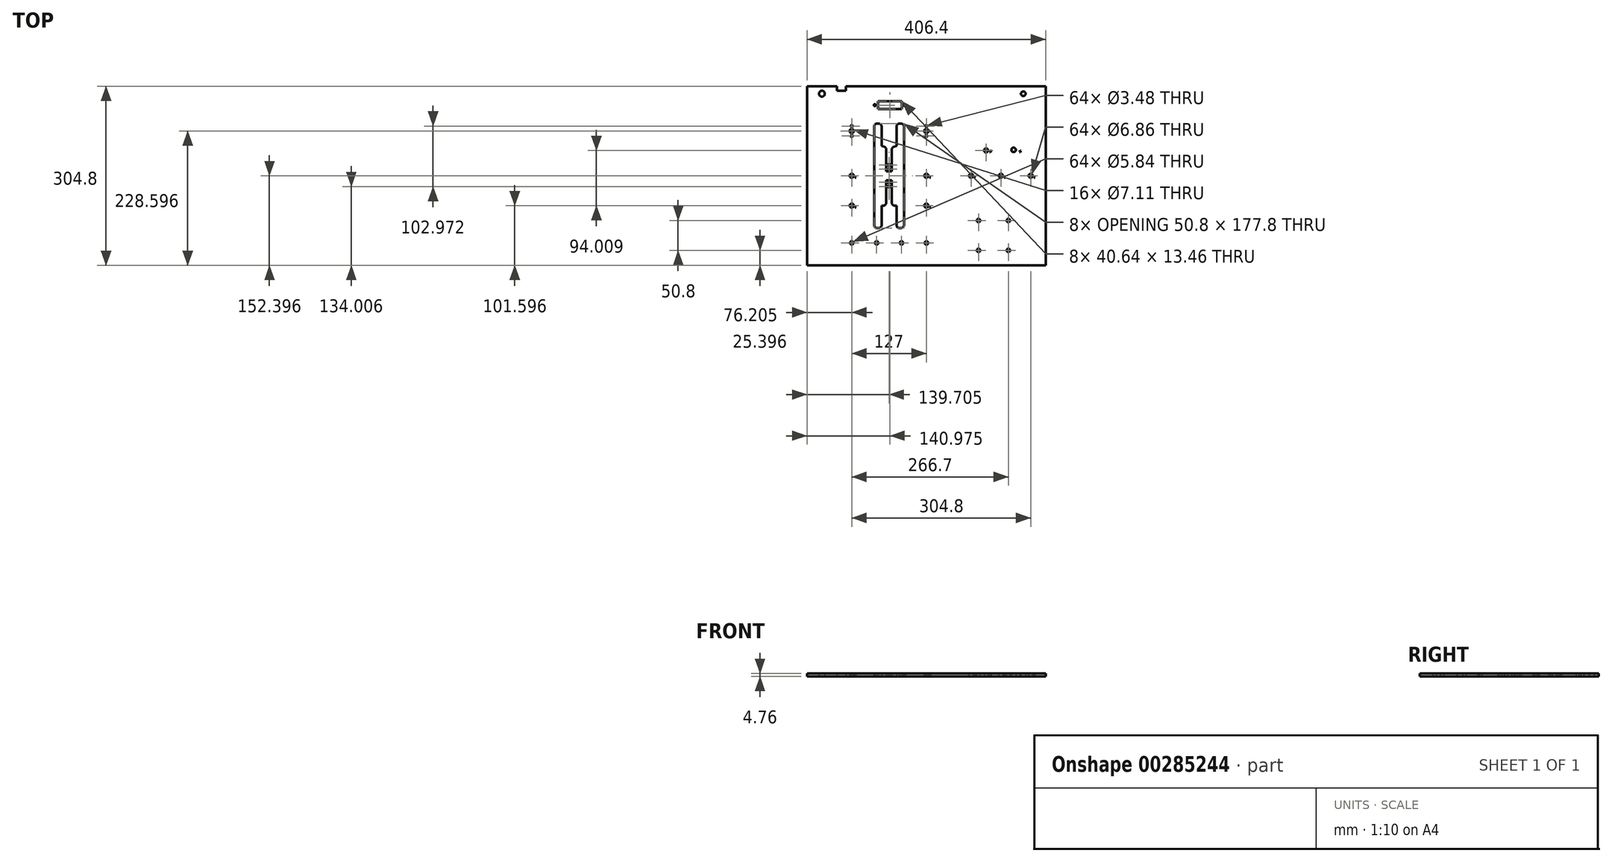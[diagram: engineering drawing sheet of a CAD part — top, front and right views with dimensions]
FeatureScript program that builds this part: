
annotation { "Feature Type Name" : "Feature", "Feature Type Description" : "" }
export const myFeature = defineFeature(function(context is Context, id is Id, definition is map)
    precondition{}
    {
        {
            var Q0;
            Q0=qCreatedBy(makeId("Top.planeOp"),FACE);
            var sketch = newSketch(context, id + "F0", { "sketchPlane" : qUnion([Q0])});
            skLineSegment(sketch, "E0.bottom", {"start": v(-218.92, 163.26) * mm, "end": v(187.48, 163.26) * mm});
            skLineSegment(sketch, "E0.top", {"start": v(-218.92, -141.54) * mm, "end": v(187.48, -141.54) * mm});
            skLineSegment(sketch, "E0.left", {"start": v(-218.92, 163.26) * mm, "end": v(-218.92, -141.54) * mm});
            skLineSegment(sketch, "E0.right", {"start": v(187.48, 163.26) * mm, "end": v(187.48, -141.54) * mm});
            skSolve(sketch);
        }
        {
            var Q0;
            Q0=makeQuery(id+"F0.imprint","IMPRINT",FACE,{"disambiguationData":[TD([[makeQuery(id+"F0.imprint","IMPRINT",EDGE,{"derivedFrom":sQuery(id+"F0.wireOp",EDGE,"E0.bottom")}),-1.0]])]});
            extrude(context, id + "F1", {"entities" : qUnion([Q0]), "depth" : 4.76 * mm});
        }
        {
            var Q0;
            Q0=qCreatedBy(makeId("Top.planeOp"),FACE);
            var sketch = newSketch(context, id + "F2", { "sketchPlane" : qUnion([Q0])});
            skCircle(sketch, "E1", {"center": v(-142.72, 87.06) * mm, "radius": 12.2 * mm, "construction": true});
            skCircle(sketch, "E2", {"center": v(-142.72, 95.44) * mm, "radius": 1.74 * mm});
            skCircle(sketch, "E3", {"center": v(-142.72, 78.67) * mm, "radius": 1.74 * mm});
            skLineSegment(sketch, "E4", {"start": v(-142.72, 87.06) * mm, "end": v(-142.72, -142.08) * mm, "construction": true});
            skCircle(sketch, "E5", {"center": v(-142.72, 10.86) * mm, "radius": 3.43 * mm});
            skCircle(sketch, "E6", {"center": v(-142.72, 87.06) * mm, "radius": 3.56 * mm});
            skLineSegment(sketch, "E7.top", {"start": v(-136.6, 8) * mm, "end": v(-135.36, 7.72) * mm});
            skLineSegment(sketch, "E7.left", {"start": v(-136.6, 8) * mm, "end": v(-136.67, 7.67) * mm});
            skLineSegment(sketch, "E7.right", {"start": v(-135.36, 7.72) * mm, "end": v(-135.44, 7.38) * mm});
            skLineSegment(sketch, "E8", {"start": v(-136.67, 7.67) * mm, "end": v(-135.44, 7.38) * mm});
            skCircle(sketch, "E9.0.1.0", {"center": v(-142.72, -39.94) * mm, "radius": 3.43 * mm});
            skLineSegment(sketch, "E9.0.1.1", {"start": v(-136.6, -42.8) * mm, "end": v(-135.36, -43.08) * mm});
            skLineSegment(sketch, "E9.0.1.2", {"start": v(-136.67, -43.13) * mm, "end": v(-135.44, -43.42) * mm});
            skLineSegment(sketch, "E9.0.1.3", {"start": v(-135.36, -43.08) * mm, "end": v(-135.44, -43.42) * mm});
            skLineSegment(sketch, "E9.0.1.4", {"start": v(-136.6, -42.8) * mm, "end": v(-136.67, -43.13) * mm});
            skLineSegment(sketch, "E9.direction1", {"start": v(-142.72, 10.86) * mm, "end": v(-117.32, 10.86) * mm, "construction": true});
            skLineSegment(sketch, "E9.direction2", {"start": v(-142.72, 10.86) * mm, "end": v(-142.72, -39.94) * mm, "construction": true});
            skCircle(sketch, "E10.1.0.0", {"center": v(-15.72, -39.94) * mm, "radius": 3.43 * mm});
            skCircle(sketch, "E10.1.0.1", {"center": v(-15.72, 87.06) * mm, "radius": 3.56 * mm});
            skCircle(sketch, "E10.1.0.2", {"center": v(-15.72, 10.86) * mm, "radius": 3.43 * mm});
            skLineSegment(sketch, "E10.1.0.3", {"start": v(-15.72, 87.06) * mm, "end": v(-15.72, -142.08) * mm, "construction": true});
            skCircle(sketch, "E10.1.0.4", {"center": v(-15.72, 87.06) * mm, "radius": 12.2 * mm, "construction": true});
            skLineSegment(sketch, "E10.1.0.5", {"start": v(-15.72, 10.86) * mm, "end": v(9.68, 10.86) * mm, "construction": true});
            skLineSegment(sketch, "E10.1.0.6", {"start": v(-15.72, 10.86) * mm, "end": v(-15.72, -39.94) * mm, "construction": true});
            skCircle(sketch, "E10.1.0.7", {"center": v(-15.72, 78.67) * mm, "radius": 1.74 * mm});
            skCircle(sketch, "E10.1.0.8", {"center": v(-15.72, 95.44) * mm, "radius": 1.74 * mm});
            skLineSegment(sketch, "E10.1.0.9", {"start": v(-8.36, 7.72) * mm, "end": v(-8.44, 7.38) * mm});
            skLineSegment(sketch, "E10.1.0.10", {"start": v(-9.67, 7.67) * mm, "end": v(-8.44, 7.38) * mm});
            skLineSegment(sketch, "E10.1.0.11", {"start": v(-9.6, 8) * mm, "end": v(-8.36, 7.72) * mm});
            skLineSegment(sketch, "E10.1.0.12", {"start": v(-8.36, -43.08) * mm, "end": v(-8.44, -43.42) * mm});
            skLineSegment(sketch, "E10.1.0.13", {"start": v(-9.6, 8) * mm, "end": v(-9.67, 7.67) * mm});
            skLineSegment(sketch, "E10.1.0.14", {"start": v(-9.6, -42.8) * mm, "end": v(-9.67, -43.13) * mm});
            skLineSegment(sketch, "E10.1.0.15", {"start": v(-9.6, -42.8) * mm, "end": v(-8.36, -43.08) * mm});
            skLineSegment(sketch, "E10.1.0.16", {"start": v(-9.67, -43.13) * mm, "end": v(-8.44, -43.42) * mm});
            skLineSegment(sketch, "E10.direction1", {"start": v(-142.72, -142.08) * mm, "end": v(-15.72, -142.08) * mm, "construction": true});
            skLineSegment(sketch, "E11.bottom", {"start": v(-168.12, 163.26) * mm, "end": v(-152.88, 163.26) * mm});
            skLineSegment(sketch, "E11.top", {"start": v(-168.12, 155.38) * mm, "end": v(-152.88, 155.38) * mm});
            skLineSegment(sketch, "E11.left", {"start": v(-168.12, 163.26) * mm, "end": v(-168.12, 155.38) * mm});
            skLineSegment(sketch, "E11.right", {"start": v(-152.88, 163.26) * mm, "end": v(-152.88, 155.38) * mm});
            skCircle(sketch, "E12", {"center": v(-193.52, 150.56) * mm, "radius": 4.95 * mm});
            skLineSegment(sketch, "E13.1.0.0", {"start": v(67.84, 7.72) * mm, "end": v(67.76, 7.38) * mm});
            skLineSegment(sketch, "E13.1.0.1", {"start": v(66.6, 8) * mm, "end": v(66.53, 7.67) * mm});
            skCircle(sketch, "E13.1.0.2", {"center": v(60.48, 10.86) * mm, "radius": 3.43 * mm});
            skLineSegment(sketch, "E13.1.0.3", {"start": v(66.6, 8) * mm, "end": v(67.84, 7.72) * mm});
            skLineSegment(sketch, "E13.1.0.4", {"start": v(66.53, 7.67) * mm, "end": v(67.76, 7.38) * mm});
            skLineSegment(sketch, "E13.direction1", {"start": v(-15.72, 10.86) * mm, "end": v(60.48, 10.86) * mm, "construction": true});
            skLineSegment(sketch, "E14.1.0.0", {"start": v(117.33, 7.67) * mm, "end": v(118.56, 7.38) * mm});
            skLineSegment(sketch, "E14.1.0.1", {"start": v(35.08, 10.86) * mm, "end": v(111.28, 10.86) * mm, "construction": true});
            skLineSegment(sketch, "E14.1.0.2", {"start": v(118.64, 7.72) * mm, "end": v(118.56, 7.38) * mm});
            skLineSegment(sketch, "E14.1.0.3", {"start": v(117.4, 8) * mm, "end": v(117.33, 7.67) * mm});
            skLineSegment(sketch, "E14.1.0.4", {"start": v(117.4, 8) * mm, "end": v(118.64, 7.72) * mm});
            skCircle(sketch, "E14.1.0.5", {"center": v(111.28, 10.86) * mm, "radius": 3.43 * mm});
            skLineSegment(sketch, "E14.2.0.0", {"start": v(168.13, 7.67) * mm, "end": v(169.36, 7.38) * mm});
            skLineSegment(sketch, "E14.2.0.1", {"start": v(85.88, 10.86) * mm, "end": v(162.08, 10.86) * mm, "construction": true});
            skLineSegment(sketch, "E14.2.0.2", {"start": v(169.44, 7.72) * mm, "end": v(169.36, 7.38) * mm});
            skLineSegment(sketch, "E14.2.0.3", {"start": v(168.2, 8) * mm, "end": v(168.13, 7.67) * mm});
            skLineSegment(sketch, "E14.2.0.4", {"start": v(168.2, 8) * mm, "end": v(169.44, 7.72) * mm});
            skCircle(sketch, "E14.2.0.5", {"center": v(162.08, 10.86) * mm, "radius": 3.43 * mm});
            skLineSegment(sketch, "E14.direction1", {"start": v(-15.72, 10.86) * mm, "end": v(35.08, 10.86) * mm, "construction": true});
            skLineSegment(sketch, "E15.1.0.0", {"start": v(92.8, 53.94) * mm, "end": v(94.04, 53.66) * mm});
            skLineSegment(sketch, "E15.1.0.2", {"start": v(94.04, 53.66) * mm, "end": v(93.41, 50.93) * mm});
            skLineSegment(sketch, "E15.1.0.3", {"start": v(92.8, 53.94) * mm, "end": v(92.17, 51.22) * mm});
            skLineSegment(sketch, "E15.1.0.4", {"start": v(92.17, 51.22) * mm, "end": v(93.41, 50.93) * mm});
            skCircle(sketch, "E15.1.0.5", {"center": v(86.05, 54.06) * mm, "radius": 3.43 * mm});
            skLineSegment(sketch, "E15.2.0.0", {"start": v(143.6, 53.94) * mm, "end": v(144.84, 53.66) * mm});
            skLineSegment(sketch, "E15.2.0.1", {"start": v(56.7, 54.98) * mm, "end": v(132.9, 54.98) * mm, "construction": true});
            skLineSegment(sketch, "E15.2.0.2", {"start": v(144.84, 53.66) * mm, "end": v(144.21, 50.93) * mm});
            skLineSegment(sketch, "E15.2.0.3", {"start": v(143.6, 53.94) * mm, "end": v(142.97, 51.22) * mm});
            skLineSegment(sketch, "E15.2.0.4", {"start": v(142.97, 51.22) * mm, "end": v(144.21, 50.93) * mm});
            skCircle(sketch, "E15.2.0.5", {"center": v(132.9, 54.98) * mm, "radius": 3.81 * mm});
            skLineSegment(sketch, "E16.bottom", {"start": v(-99.54, 99.76) * mm, "end": v(-97, 99.76) * mm});
            skLineSegment(sketch, "E16.top", {"start": v(-99.54, -78.04) * mm, "end": v(-97, -78.04) * mm});
            skLineSegment(sketch, "E16.left", {"start": v(-104.62, 94.68) * mm, "end": v(-104.62, -72.96) * mm});
            skLineSegment(sketch, "E16.right", {"start": v(-53.82, 94.68) * mm, "end": v(-53.82, -72.96) * mm});
            skLineSegment(sketch, "E17.left", {"start": v(-91.92, 94.68) * mm, "end": v(-91.92, 61.66) * mm});
            skLineSegment(sketch, "E17.right", {"start": v(-66.52, 94.68) * mm, "end": v(-66.52, 61.66) * mm});
            skLineSegment(sketch, "E18.left", {"start": v(-91.92, 76.83) * mm, "end": v(-91.92, 77.38) * mm, "construction": true});
            skLineSegment(sketch, "E18.right", {"start": v(-104.62, 76.83) * mm, "end": v(-104.62, 77.38) * mm, "construction": true});
            skLineSegment(sketch, "E19.trimOffspring", {"start": v(-61.44, 99.76) * mm, "end": v(-58.9, 99.76) * mm});
            skLineSegment(sketch, "E20.bottom", {"start": v(-83.88, 18.48) * mm, "end": v(-74.55, 18.48) * mm});
            skLineSegment(sketch, "E20.top", {"start": v(-83.88, 3.24) * mm, "end": v(-74.55, 3.24) * mm});
            skLineSegment(sketch, "E21", {"start": v(-83.88, 18.48) * mm, "end": v(-83.88, 55.4) * mm});
            skLineSegment(sketch, "E22", {"start": v(-87.43, 60.24) * mm, "end": v(-91.92, 61.66) * mm});
            skLineSegment(sketch, "E23", {"start": v(-79.22, 18.48) * mm, "end": v(-79.22, 3.24) * mm, "construction": true});
            skLineSegment(sketch, "E24.MirrorCS", {"start": v(-83.88, 3.24) * mm, "end": v(-83.88, -34.86) * mm});
            skLineSegment(sketch, "E25.MirrorCS", {"start": v(-88.96, -39.94) * mm, "end": v(-89.6, -39.94) * mm});
            skLineSegment(sketch, "E26.MirrorCS", {"start": v(-88.96, -39.94) * mm, "end": v(-91.92, -39.94) * mm});
            skLineSegment(sketch, "E27.MirrorCS", {"start": v(-83.88, 1.2) * mm, "end": v(-83.88, -34.86) * mm});
            skPoint(sketch, "E28.MirrorCS.start.orphan", {"position": v(-79.85, 59.12) * mm});
            skLineSegment(sketch, "E29.trimOffspring", {"start": v(-91.92, -39.94) * mm, "end": v(-91.92, -72.96) * mm});
            skPoint(sketch, "E30.MirrorP", {"position": v(-78.58, 59.12) * mm});
            skLineSegment(sketch, "E31.MirrorCS", {"start": v(-71, 60.24) * mm, "end": v(-66.52, 61.66) * mm});
            skLineSegment(sketch, "E32.MirrorCS", {"start": v(-74.55, 18.48) * mm, "end": v(-74.55, 55.4) * mm});
            skLineSegment(sketch, "E33.MirrorCS", {"start": v(-74.55, 3.24) * mm, "end": v(-74.55, -34.86) * mm});
            skLineSegment(sketch, "E34.MirrorCS", {"start": v(-69.47, -39.94) * mm, "end": v(-68.82, -39.94) * mm});
            skLineSegment(sketch, "E35.trimOffspring", {"start": v(-66.52, -39.94) * mm, "end": v(-66.52, -72.96) * mm});
            skArc(sketch, "E36.filletArc", {"start": v(-83.88, 55.4) * mm, "mid": v(-84.86, 58.4) * mm, "end": v(-87.43, 60.24) * mm});
            skArc(sketch, "E37.filletArc", {"start": v(-71, 60.24) * mm, "mid": v(-73.57, 58.4) * mm, "end": v(-74.55, 55.4) * mm});
            skArc(sketch, "E38.filletArc", {"start": v(-88.96, -39.94) * mm, "mid": v(-85.36, -38.46) * mm, "end": v(-83.88, -34.86) * mm});
            skArc(sketch, "E39.filletArc", {"start": v(-74.55, -34.86) * mm, "mid": v(-73.07, -38.46) * mm, "end": v(-69.47, -39.94) * mm});
            skLineSegment(sketch, "E40.trimOffspring", {"start": v(-61.44, -78.04) * mm, "end": v(-58.9, -78.04) * mm});
            skPoint(sketch, "E41.visualSharp", {"position": v(-91.92, 99.76) * mm});
            skArc(sketch, "E41.filletArc", {"start": v(-91.92, 94.68) * mm, "mid": v(-93.4, 98.27) * mm, "end": v(-97, 99.76) * mm});
            skPoint(sketch, "E42.visualSharp", {"position": v(-104.62, 99.76) * mm});
            skArc(sketch, "E42.filletArc", {"start": v(-99.54, 99.76) * mm, "mid": v(-103.13, 98.27) * mm, "end": v(-104.62, 94.68) * mm});
            skPoint(sketch, "E43.visualSharp", {"position": v(-91.92, -78.04) * mm});
            skArc(sketch, "E43.filletArc", {"start": v(-97, -78.04) * mm, "mid": v(-93.4, -76.56) * mm, "end": v(-91.92, -72.96) * mm});
            skPoint(sketch, "E44.visualSharp", {"position": v(-104.62, -78.04) * mm});
            skArc(sketch, "E44.filletArc", {"start": v(-104.62, -72.96) * mm, "mid": v(-103.13, -76.56) * mm, "end": v(-99.54, -78.04) * mm});
            skPoint(sketch, "E45.visualSharp", {"position": v(-66.52, -78.04) * mm});
            skArc(sketch, "E45.filletArc", {"start": v(-66.52, -72.96) * mm, "mid": v(-65.03, -76.56) * mm, "end": v(-61.44, -78.04) * mm});
            skPoint(sketch, "E46.visualSharp", {"position": v(-53.82, -78.04) * mm});
            skArc(sketch, "E46.filletArc", {"start": v(-58.9, -78.04) * mm, "mid": v(-55.3, -76.56) * mm, "end": v(-53.82, -72.96) * mm});
            skPoint(sketch, "E47.visualSharp", {"position": v(-66.52, 99.76) * mm});
            skArc(sketch, "E47.filletArc", {"start": v(-61.44, 99.76) * mm, "mid": v(-65.03, 98.27) * mm, "end": v(-66.52, 94.68) * mm});
            skPoint(sketch, "E48.visualSharp", {"position": v(-53.82, 99.76) * mm});
            skArc(sketch, "E48.filletArc", {"start": v(-53.82, 94.68) * mm, "mid": v(-55.3, 98.27) * mm, "end": v(-58.9, 99.76) * mm});
            skLineSegment(sketch, "E49", {"start": v(-68.82, -39.94) * mm, "end": v(-66.52, -39.94) * mm});
            skCircle(sketch, "E50", {"center": v(-79.22, 21.93) * mm, "radius": 1.74 * mm});
            skCircle(sketch, "E51", {"center": v(-79.22, 29.25) * mm, "radius": 1.74 * mm});
            skLineSegment(sketch, "E52", {"start": v(-83.88, 33.44) * mm, "end": v(-74.55, 33.44) * mm, "construction": true});
            skLineSegment(sketch, "E53", {"start": v(-74.55, 33.44) * mm, "end": v(-74.55, -11.72) * mm, "construction": true});
            skLineSegment(sketch, "E54", {"start": v(-74.55, -11.72) * mm, "end": v(-83.88, -11.72) * mm, "construction": true});
            skLineSegment(sketch, "E55", {"start": v(-83.88, -11.72) * mm, "end": v(-83.88, 33.44) * mm, "construction": true});
            skLineSegment(sketch, "E56", {"start": v(-79.22, 10.86) * mm, "end": v(-87.64, 10.86) * mm, "construction": true});
            skCircle(sketch, "E57.MirrorC", {"center": v(-79.22, -7.53) * mm, "radius": 1.74 * mm});
            skCircle(sketch, "E58.MirrorC", {"center": v(-79.22, -0.22) * mm, "radius": 1.74 * mm});
            skCircle(sketch, "E59", {"center": v(149.38, 150.56) * mm, "radius": 3.94 * mm});
            skLineSegment(sketch, "E60.bottom", {"start": v(-98.27, 137.86) * mm, "end": v(-57.63, 137.86) * mm});
            skLineSegment(sketch, "E60.top", {"start": v(-98.27, 124.4) * mm, "end": v(-57.63, 124.4) * mm});
            skLineSegment(sketch, "E60.left", {"start": v(-98.27, 137.86) * mm, "end": v(-98.27, 124.4) * mm});
            skLineSegment(sketch, "E60.right", {"start": v(-57.63, 137.86) * mm, "end": v(-57.63, 124.4) * mm});
            skCircle(sketch, "E61", {"center": v(-52.55, 131.12) * mm, "radius": 1.65 * mm});
            skLineSegment(sketch, "E62", {"start": v(-77.95, 137.86) * mm, "end": v(-77.95, 124.4) * mm, "construction": true});
            skCircle(sketch, "E63.MirrorC", {"center": v(-103.35, 131.12) * mm, "radius": 1.65 * mm});
            skSolve(sketch);
        }
        {
            var Q0;
            Q0 = qSketchRegion(id + "F2", true);
            extrude(context, id + "F3", {"entities" : qUnion([Q0]), "operationType" : NewBodyOperationType.REMOVE, "depth" : 25.4 * mm});
        }
        {
            var Q0;
            Q0=makeQuery(id+"F1.opExtrude","CAP_FACE",FACE,{"disambiguationData":[OSD([sQuery(id+"F0.wireOp",EDGE,"E0.bottom"),sQuery(id+"F0.wireOp",EDGE,"E0.top"),sQuery(id+"F0.wireOp",EDGE,"E0.left"),sQuery(id+"F0.wireOp",EDGE,"E0.right")])],"isStart":false});
            var sketch = newSketch(context, id + "F4", { "sketchPlane" : qUnion([Q0])});
            skCircle(sketch, "E64", {"center": v(-142.72, -103.44) * mm, "radius": 2.92 * mm});
            skCircle(sketch, "E65.1.0.0", {"center": v(-100.3, -103.44) * mm, "radius": 2.92 * mm});
            skLineSegment(sketch, "E65.direction1", {"start": v(-142.72, -103.44) * mm, "end": v(-100.3, -103.44) * mm, "construction": true});
            skCircle(sketch, "E66", {"center": v(73.18, -65.34) * mm, "radius": 2.92 * mm});
            skCircle(sketch, "E67.0.1.0", {"center": v(73.18, -116.14) * mm, "radius": 2.92 * mm});
            skCircle(sketch, "E67.1.0.0", {"center": v(123.98, -65.34) * mm, "radius": 2.92 * mm});
            skCircle(sketch, "E67.1.1.0", {"center": v(123.98, -116.14) * mm, "radius": 2.92 * mm});
            skLineSegment(sketch, "E67.direction1", {"start": v(73.18, -71.7) * mm, "end": v(123.98, -71.7) * mm, "construction": true});
            skLineSegment(sketch, "E67.direction2", {"start": v(73.18, -71.7) * mm, "end": v(73.18, -122.5) * mm, "construction": true});
            skCircle(sketch, "E68.0.2.0", {"center": v(-57.88, -103.44) * mm, "radius": 2.92 * mm});
            skCircle(sketch, "E68.0.3.0", {"center": v(-15.46, -103.44) * mm, "radius": 2.92 * mm});
            skSolve(sketch);
        }
        {
            var Q0;
            Q0 = qSketchRegion(id + "F4", true);
            extrude(context, id + "F5", {"entities" : qUnion([Q0]), "operationType" : NewBodyOperationType.REMOVE, "oppositeDirection" : true, "depth" : 25.4 * mm});
        }
    });
